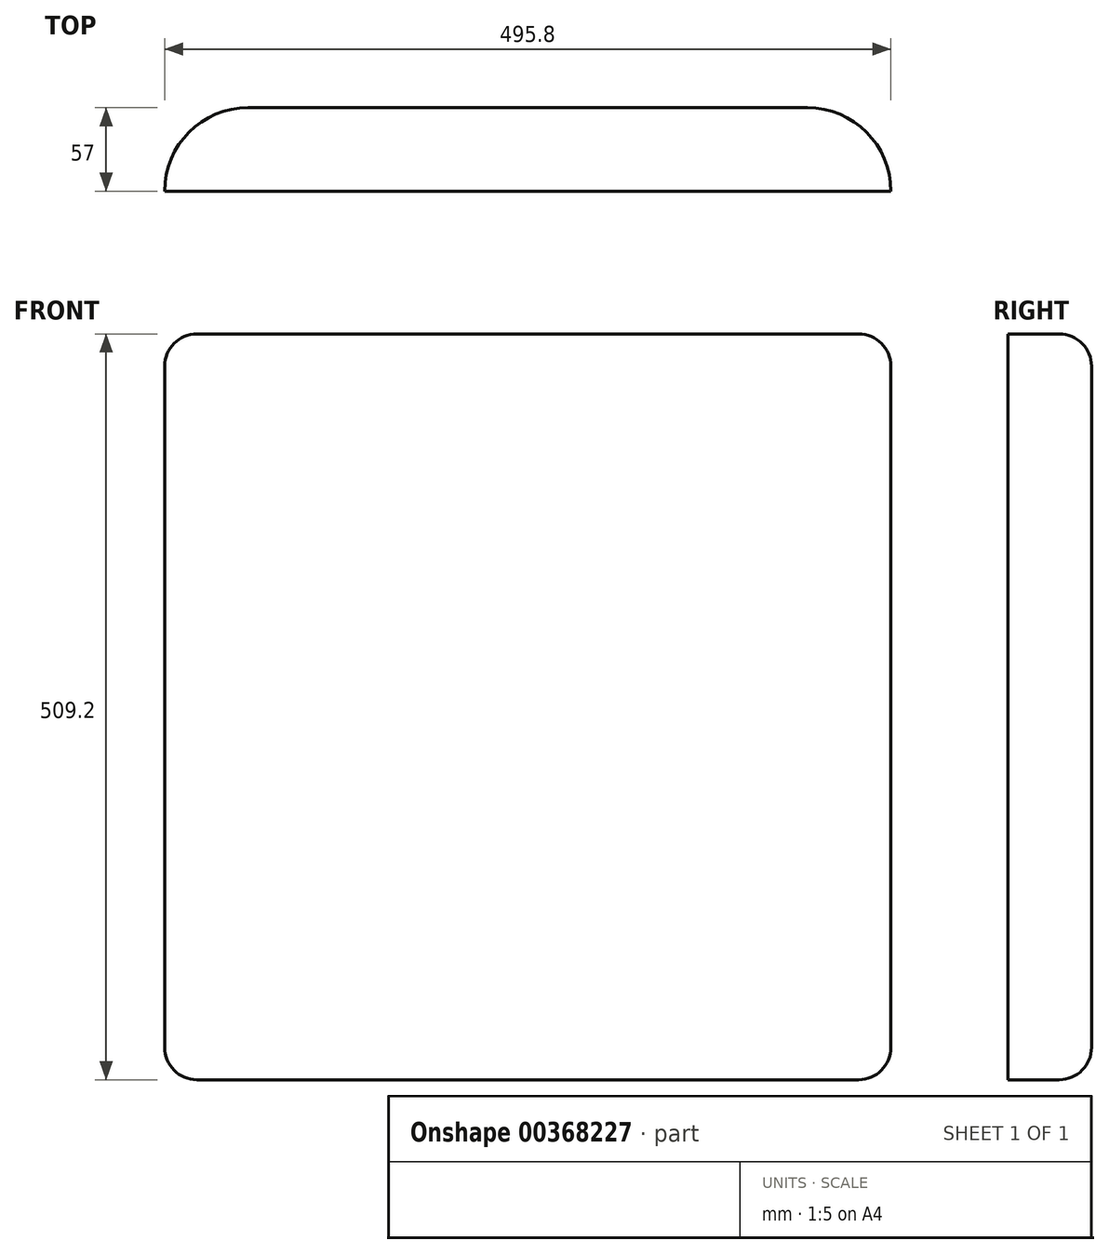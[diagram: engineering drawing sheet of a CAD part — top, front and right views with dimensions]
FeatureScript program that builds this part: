
annotation { "Feature Type Name" : "Feature", "Feature Type Description" : "" }
export const myFeature = defineFeature(function(context is Context, id is Id, definition is map)
    precondition{}
    {
        {
            var Q0;
            Q0=qCreatedBy(makeId("Top.planeOp"),FACE);
            var sketch = newSketch(context, id + "F0", { "sketchPlane" : qUnion([Q0])});
            skLineSegment(sketch, "E0.bottom", {"start": v(0, 0) * mm, "end": v(495.8, 0) * mm});
            skLineSegment(sketch, "E0.top", {"start": v(0, 57) * mm, "end": v(495.8, 57) * mm});
            skLineSegment(sketch, "E0.left", {"start": v(0, 0) * mm, "end": v(0, 57) * mm});
            skLineSegment(sketch, "E0.right", {"start": v(495.8, 0) * mm, "end": v(495.8, 57) * mm});
            skSolve(sketch);
        }
        {
            var Q0;
            Q0 = qSketchRegion(id + "F0", true);
            extrude(context, id + "F1", {"entities" : qUnion([Q0]), "oppositeDirection" : true, "depth" : 509.2 * mm, "offsetDistance" : 25 * mm});
        }
        {
            var Q0;
            Q0=makeQuery(id+"F1.opExtrude","SWEPT_EDGE",EDGE,{"disambiguationData":[OSD([sQuery(id+"F0.wireOp",EDGE,"E0.top"),sQuery(id+"F0.wireOp",EDGE,"E0.right")])]});
            var Q1;
            Q1=makeQuery(id+"F1.opExtrude","SWEPT_EDGE",EDGE,{"disambiguationData":[OSD([sQuery(id+"F0.wireOp",EDGE,"E0.top"),sQuery(id+"F0.wireOp",EDGE,"E0.left")])]});
            fillet(context, id + "F2", {"entities" : qUnion([Q0, Q1]), "radius" : 57 * mm, "tangentPropagation" : true, "allowEdgeOverflow" : false});
        }
        {
            var Q0;
            {var subQ0=sQuery(id+"F0.wireOp",EDGE,"E0.right");var subQ1=sQuery(id+"F0.wireOp",EDGE,"E0.top");Q0=makeQuery(id+"F2.opFillet","BLEND_EDGE",EDGE,{"blendedFrom":[makeQuery(id+"F1.opExtrude","SWEPT_EDGE",EDGE,{"disambiguationData":[OSD([subQ1,subQ0])]}),makeQuery(id+"F1.opExtrude","CAP_FACE",FACE,{"disambiguationData":[OSD([sQuery(id+"F0.wireOp",EDGE,"E0.bottom"),subQ1,sQuery(id+"F0.wireOp",EDGE,"E0.left"),subQ0])],"isStart":true})],"blendedInto":[makeQuery(id+"F1.opExtrude","CAP_FACE",FACE,{"disambiguationData":[OSD([sQuery(id+"F0.wireOp",EDGE,"E0.bottom"),subQ1,sQuery(id+"F0.wireOp",EDGE,"E0.left"),subQ0])],"isStart":true})]});}
            var Q1;
            Q1=makeQuery(id+"F1.opExtrude","CAP_EDGE",EDGE,{"disambiguationData":[OSD([sQuery(id+"F0.wireOp",EDGE,"E0.top")])],"isStart":true});
            var Q2;
            {var subQ0=sQuery(id+"F0.wireOp",EDGE,"E0.left");var subQ1=sQuery(id+"F0.wireOp",EDGE,"E0.top");Q2=makeQuery(id+"F2.opFillet","BLEND_EDGE",EDGE,{"blendedFrom":[makeQuery(id+"F1.opExtrude","SWEPT_EDGE",EDGE,{"disambiguationData":[OSD([subQ1,subQ0])]}),makeQuery(id+"F1.opExtrude","CAP_FACE",FACE,{"disambiguationData":[OSD([sQuery(id+"F0.wireOp",EDGE,"E0.bottom"),subQ1,subQ0,sQuery(id+"F0.wireOp",EDGE,"E0.right")])],"isStart":true})],"blendedInto":[makeQuery(id+"F1.opExtrude","CAP_FACE",FACE,{"disambiguationData":[OSD([sQuery(id+"F0.wireOp",EDGE,"E0.bottom"),subQ1,subQ0,sQuery(id+"F0.wireOp",EDGE,"E0.right")])],"isStart":true})]});}
            var Q3;
            Q3=makeQuery(id+"F1.opExtrude","CAP_EDGE",EDGE,{"disambiguationData":[OSD([sQuery(id+"F0.wireOp",EDGE,"E0.top")])],"isStart":false});
            var Q4;
            {var subQ0=sQuery(id+"F0.wireOp",EDGE,"E0.left");var subQ1=sQuery(id+"F0.wireOp",EDGE,"E0.top");Q4=makeQuery(id+"F2.opFillet","BLEND_EDGE",EDGE,{"blendedFrom":[makeQuery(id+"F1.opExtrude","SWEPT_EDGE",EDGE,{"disambiguationData":[OSD([subQ1,subQ0])]}),makeQuery(id+"F1.opExtrude","CAP_FACE",FACE,{"disambiguationData":[OSD([sQuery(id+"F0.wireOp",EDGE,"E0.bottom"),subQ1,subQ0,sQuery(id+"F0.wireOp",EDGE,"E0.right")])],"isStart":false})],"blendedInto":[makeQuery(id+"F1.opExtrude","CAP_FACE",FACE,{"disambiguationData":[OSD([sQuery(id+"F0.wireOp",EDGE,"E0.bottom"),subQ1,subQ0,sQuery(id+"F0.wireOp",EDGE,"E0.right")])],"isStart":false})]});}
            var Q5;
            {var subQ0=sQuery(id+"F0.wireOp",EDGE,"E0.right");var subQ1=sQuery(id+"F0.wireOp",EDGE,"E0.top");Q5=makeQuery(id+"F2.opFillet","BLEND_EDGE",EDGE,{"blendedFrom":[makeQuery(id+"F1.opExtrude","SWEPT_EDGE",EDGE,{"disambiguationData":[OSD([subQ1,subQ0])]}),makeQuery(id+"F1.opExtrude","CAP_FACE",FACE,{"disambiguationData":[OSD([sQuery(id+"F0.wireOp",EDGE,"E0.bottom"),subQ1,sQuery(id+"F0.wireOp",EDGE,"E0.left"),subQ0])],"isStart":false})],"blendedInto":[makeQuery(id+"F1.opExtrude","CAP_FACE",FACE,{"disambiguationData":[OSD([sQuery(id+"F0.wireOp",EDGE,"E0.bottom"),subQ1,sQuery(id+"F0.wireOp",EDGE,"E0.left"),subQ0])],"isStart":false})]});}
            fillet(context, id + "F3", {"entities" : qUnion([Q0, Q1, Q2, Q3, Q4, Q5]), "radius" : 22 * mm, "tangentPropagation" : true, "allowEdgeOverflow" : false});
        }
    });
